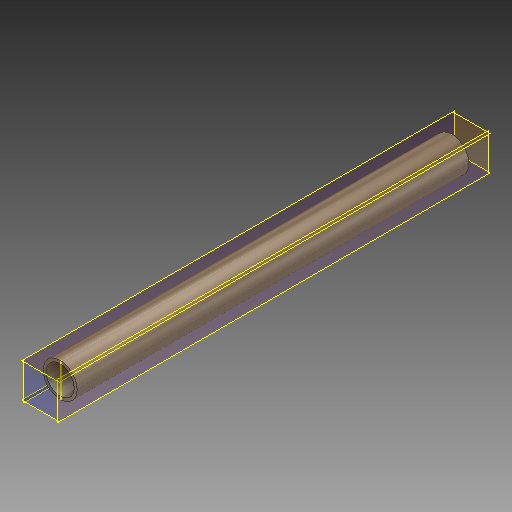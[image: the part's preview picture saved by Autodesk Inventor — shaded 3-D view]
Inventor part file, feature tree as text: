
AUTODESK INVENTOR PART (.ipt)
format: ipt  version: 2018 (Build 220112000, 112)  size: 110,080 bytes
history: native  units: mm
features: other x5, sketch x2, extrude x1
ambient origin geometry x8: Origin, YZ Plane, XZ Plane, XY Plane, X Axis, Y Axis, Z Axis, Center Point
bodies: Body1 (feature_tree)
feature tree (8):
  other  "ソリッド1"
  extrude  "押し出し1"  Depth=27.2mm
  other  "作業平面1"
  other  "作業平面2"
  other  "作業平面3"
  other  "作業平面4"
  sketch  "スケッチ2"
  sketch  "スケッチ1"
